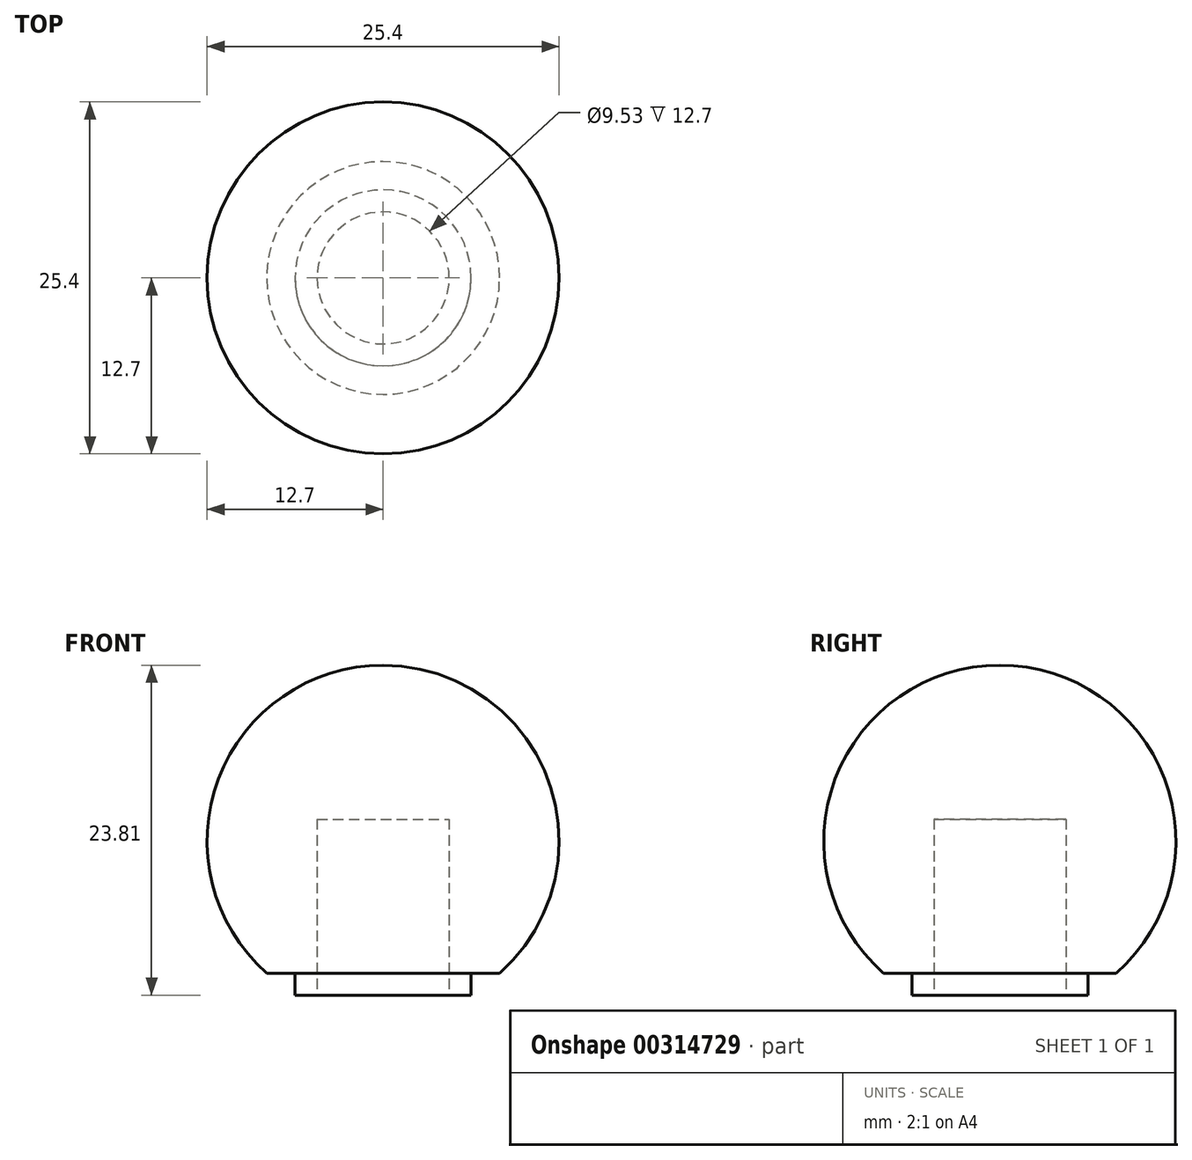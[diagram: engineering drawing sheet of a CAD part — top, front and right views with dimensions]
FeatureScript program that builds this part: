
annotation { "Feature Type Name" : "Feature", "Feature Type Description" : "" }
export const myFeature = defineFeature(function(context is Context, id is Id, definition is map)
    precondition{}
    {
        {
            var Q0;
            Q0=qCreatedBy(makeId("Front.planeOp"),FACE);
            var sketch = newSketch(context, id + "F0", { "sketchPlane" : qUnion([Q0])});
            skLineSegment(sketch, "E0", {"start": v(0, 12.7) * mm, "end": v(0, -9.52) * mm});
            skArc(sketch, "E1", {"start": v(8.4, -9.53) * mm, "mid": v(11.88, 4.5) * mm, "end": v(0, 12.7) * mm});
            skLineSegment(sketch, "E2", {"start": v(0, -9.53) * mm, "end": v(8.4, -9.53) * mm});
            skSolve(sketch);
        }
        {
            var Q0;
            Q0 = qSketchRegion(id + "F0", true);
            var Q1;
            Q1=sQuery(id+"F0.wireOp",EDGE,"E0");
            revolve(context, id + "F1", {"entities" : qUnion([Q0]), "axis" : qUnion([Q1]), "revolveType" : RevolveType.FULL});
        }
        {
            var Q0;
            Q0=makeQuery(id+"F1.opRevolve","SWEPT_FACE",FACE,{"disambiguationData":[OSD([sQuery(id+"F0.wireOp",EDGE,"E2")])]});
            var sketch = newSketch(context, id + "F2", { "sketchPlane" : qUnion([Q0])});
            skCircle(sketch, "E3", {"center": v(0, 0) * mm, "radius": 6.35 * mm});
            skSolve(sketch);
        }
        {
            var Q0;
            Q0 = qSketchRegion(id + "F2", true);
            extrude(context, id + "F3", {"entities" : qUnion([Q0]), "operationType" : NewBodyOperationType.ADD, "depth" : 1.59 * mm});
        }
        {
            var Q0;
            Q0=makeQuery(id+"F3.opExtrude","CAP_FACE",FACE,{"disambiguationData":[OSD([sQuery(id+"F2.wireOp",EDGE,"E3")])],"isStart":false});
            var sketch = newSketch(context, id + "F4", { "sketchPlane" : qUnion([Q0])});
            skCircle(sketch, "E4", {"center": v(0, 0) * mm, "radius": 4.76 * mm});
            skSolve(sketch);
        }
        {
            var Q0;
            Q0 = qSketchRegion(id + "F4", true);
            extrude(context, id + "F5", {"entities" : qUnion([Q0]), "operationType" : NewBodyOperationType.REMOVE, "oppositeDirection" : true, "depth" : 12.7 * mm});
        }
    });
